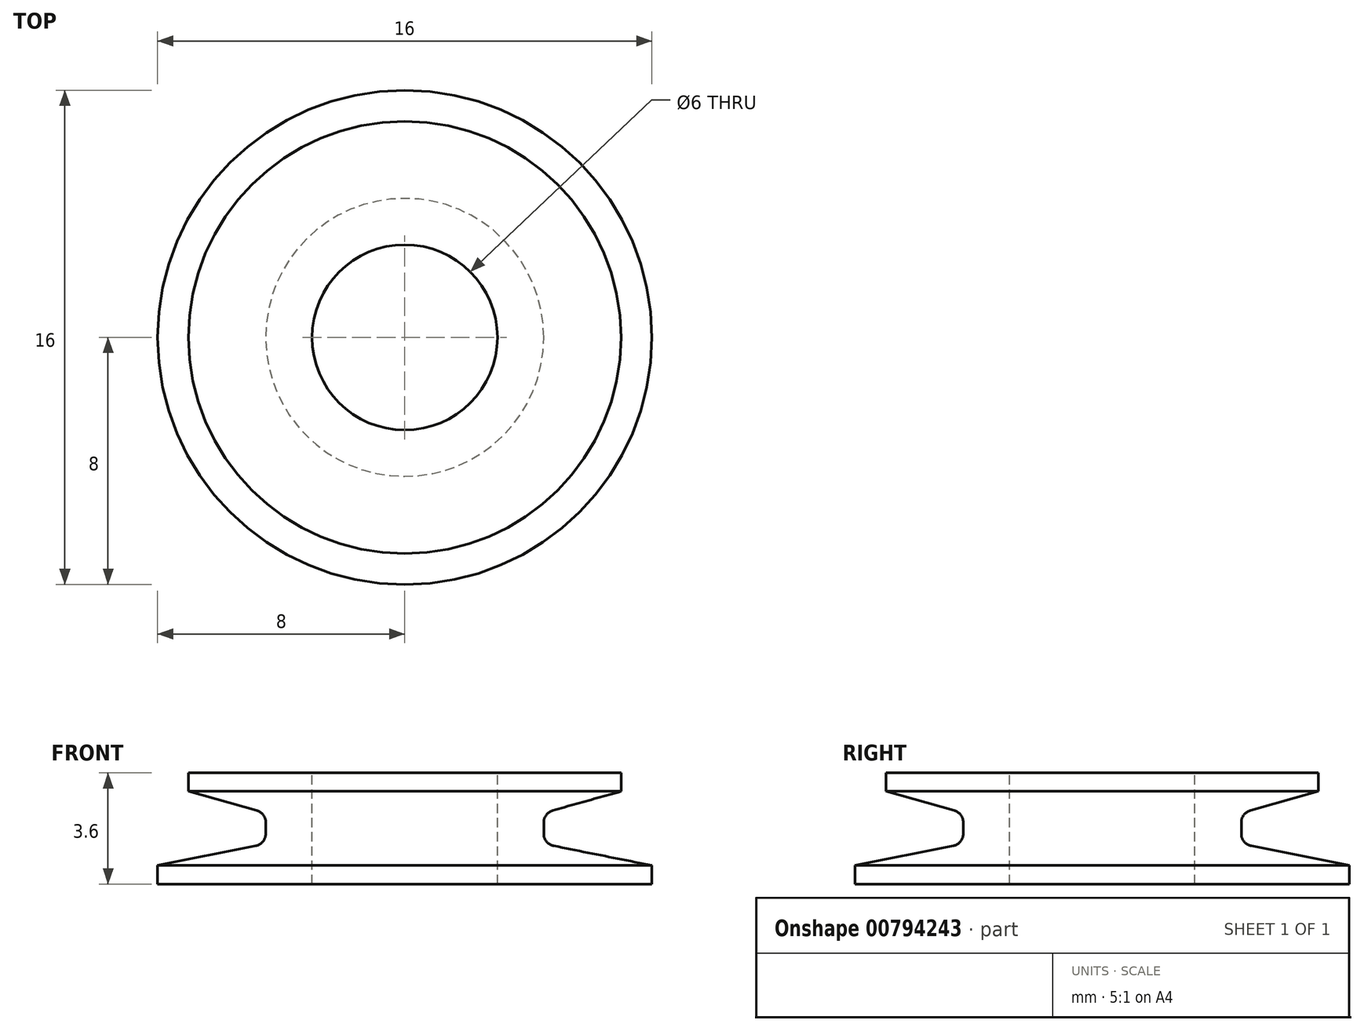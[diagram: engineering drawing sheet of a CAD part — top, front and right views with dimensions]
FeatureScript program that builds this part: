
annotation { "Feature Type Name" : "Feature", "Feature Type Description" : "" }
export const myFeature = defineFeature(function(context is Context, id is Id, definition is map)
    precondition{}
    {
        {
            var Q0;
            Q0=qCreatedBy(makeId("Front.planeOp"),FACE);
            var sketch = newSketch(context, id + "F0", { "sketchPlane" : qUnion([Q0])});
            skLineSegment(sketch, "E0", {"start": v(0, 5.94) * mm, "end": v(0, -5.29) * mm, "construction": true});
            skLineSegment(sketch, "E1", {"start": v(3, 0) * mm, "end": v(3, 3.6) * mm});
            skLineSegment(sketch, "E2", {"start": v(3, 3.6) * mm, "end": v(7, 3.6) * mm});
            skLineSegment(sketch, "E3", {"start": v(7, 3.6) * mm, "end": v(7, 3) * mm});
            skLineSegment(sketch, "E4", {"start": v(7, 3) * mm, "end": v(4.8, 2.38) * mm});
            skLineSegment(sketch, "E5", {"start": v(4.5, 2) * mm, "end": v(4.5, 1.63) * mm});
            skLineSegment(sketch, "E6", {"start": v(4.82, 1.24) * mm, "end": v(8, 0.6) * mm});
            skLineSegment(sketch, "E7", {"start": v(8, 0.6) * mm, "end": v(8, 0) * mm});
            skLineSegment(sketch, "E8", {"start": v(8, 0) * mm, "end": v(3, 0) * mm});
            skPoint(sketch, "E9.visualSharp", {"position": v(4.5, 2.3) * mm});
            skArc(sketch, "E9.filletArc", {"start": v(4.8, 2.38) * mm, "mid": v(4.58, 2.24) * mm, "end": v(4.5, 2) * mm});
            skPoint(sketch, "E10.visualSharp", {"position": v(4.5, 1.3) * mm});
            skArc(sketch, "E10.filletArc", {"start": v(4.5, 1.63) * mm, "mid": v(4.6, 1.37) * mm, "end": v(4.82, 1.24) * mm});
            skSolve(sketch);
        }
        {
            var Q0;
            Q0 = qSketchRegion(id + "F0", true);
            var Q1;
            Q1=sQuery(id+"F0.wireOp",EDGE,"E0");
            revolve(context, id + "F1", {"surfaceOperationType" : NewSurfaceOperationType.NEW, "entities" : qUnion([Q0]), "axis" : qUnion([Q1]), "revolveType" : RevolveType.FULL});
        }
    });
